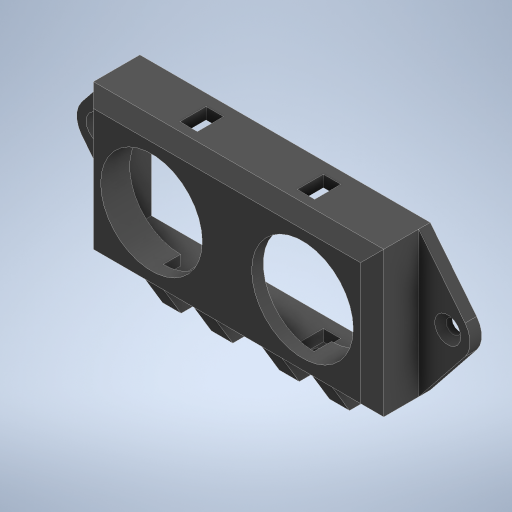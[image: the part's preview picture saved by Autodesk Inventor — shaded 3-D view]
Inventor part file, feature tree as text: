
AUTODESK INVENTOR PART (.ipt)
format: ipt  version: 2024.2 (Build 282272000, 272)  size: 418,816 bytes
history: native  units: mm
features: extrude x9, sketch x9, chamfer x2, plane x2, fillet x1
ambient origin geometry x8: Origin, YZ Plane, XZ Plane, XY Plane, X Axis, Y Axis, Z Axis, Center Point
bodies: Solid1 (feature_tree)
feature tree (23):
  extrude  "Extrusion1"  Depth=17.5mm
  extrude  "Extrusion2"  Depth=50.0mm
  extrude  "Extrusion3"  Depth=12.0mm
  chamfer  "Chamfer2"  Distance=2.0mm
  extrude  "Extrusion4"  Depth=46.0mm
  extrude  "Extrusion5"  Depth=8.0mm TaperAngle=0.0deg
  fillet  "Fillet1"  Radius=25.0mm
  chamfer  "Chamfer3"  Distance=3.0mm
  plane  "Work Plane2"
  extrude  "Extrusion6"  Depth=3.0mm
  plane  "Work Plane4"
  extrude  "Extrusion7"  Depth=17.2mm
  extrude  "Extrusion8"  Depth=1.5mm
  extrude  "Extrusion9"  Depth=3.0mm TaperAngle=0.0deg
  sketch  "Sketch1"  dims[d0=17.5mm d1=17.5mm]
  sketch  "Sketch2"  dims[d2=26.0mm d3=50.0mm]
  sketch  "Sketch3"  dims[d4=25.0mm d5=12.0mm]
  sketch  "Sketch5"  dims[d6=12.5mm d7=2.0mm d8=0.0mm]
  sketch  "Sketch6"  dims[d12=2.0mm d14=46.0mm]
  sketch  "Sketch8"  dims[d15=2.0mm d16=21.0mm d17=8.0mm d18=0.0mm d23=25.0mm d24=3.0mm d25=0.0mm]
  sketch  "Sketch10"  dims[d26=2.0mm d27=2.0mm d28=45.0deg d29=3.0mm]
  sketch  "Sketch13"  dims[d31=3.0mm d33=17.2mm]
  sketch  "Sketch14"  dims[d34=13.4mm d35=1.5mm d36=3.0mm d37=0.0mm d38=2.0mm d39=1.5mm d40=10.0mm d41=2.5mm d42=5.0mm d43=2.0mm d44=0.0mm d45=4.0mm d47=10.0mm d48=2.5mm d49=5.0mm d50=1.0mm d51=2.0mm d52=45.0deg d54=-8.9mm d56=5.0mm d57=5.0mm d58=12.1mm d59=0.0mm d60=-8.9mm d61=12.1mm d62=0.0mm d64=2.0mm d65=5.2mm d66=3.45mm d67=3.7mm d68=5.2mm d69=5.0mm d70=0.0mm d71=2.3mm d72=2.5mm d73=2.5mm d74=0.0mm d75=0.0mm d63=0.5mm]
